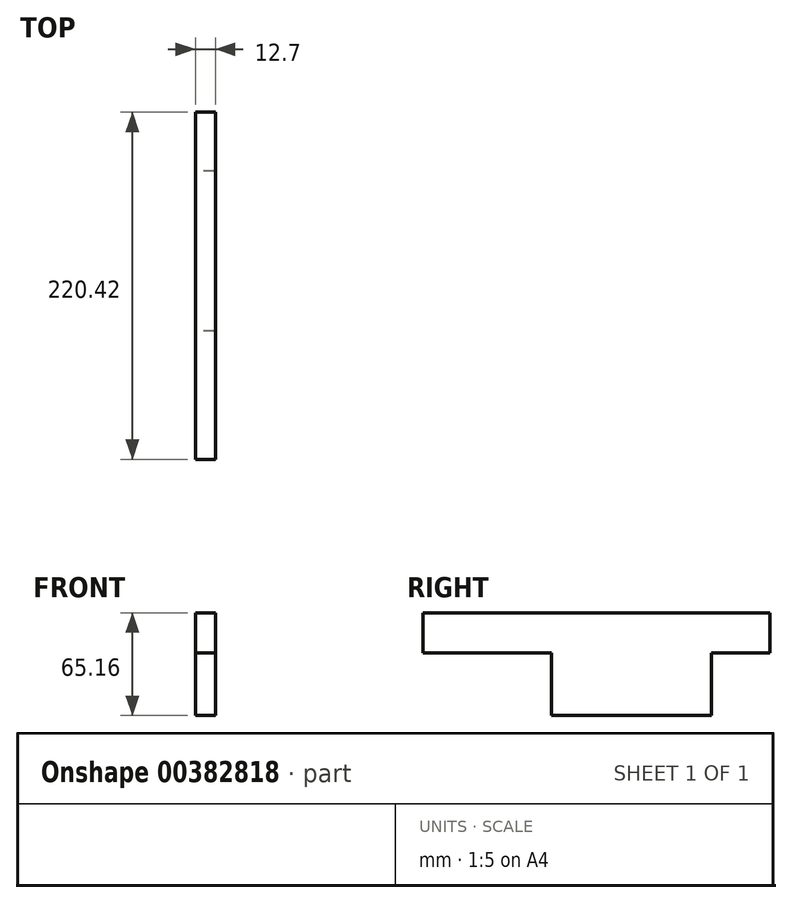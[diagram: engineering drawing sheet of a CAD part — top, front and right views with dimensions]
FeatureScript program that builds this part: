
annotation { "Feature Type Name" : "Feature", "Feature Type Description" : "" }
export const myFeature = defineFeature(function(context is Context, id is Id, definition is map)
    precondition{}
    {
        {
            var Q0;
            Q0=qCreatedBy(makeId("Right.planeOp"),FACE);
            var sketch = newSketch(context, id + "F0", { "sketchPlane" : qUnion([Q0])});
            skLineSegment(sketch, "E0", {"start": v(16.65, 65.16) * mm, "end": v(16.65, 0) * mm});
            skLineSegment(sketch, "E1", {"start": v(16.65, 65.16) * mm, "end": v(118.25, 65.16) * mm});
            skLineSegment(sketch, "E2", {"start": v(118.25, 65.16) * mm, "end": v(118.25, 0) * mm});
            skLineSegment(sketch, "E3", {"start": v(118.25, 0) * mm, "end": v(16.65, 0) * mm});
            skLineSegment(sketch, "E4", {"start": v(16.65, 65.16) * mm, "end": v(-64.92, 65.16) * mm});
            skLineSegment(sketch, "E5", {"start": v(-64.92, 65.16) * mm, "end": v(-64.92, 39.76) * mm});
            skLineSegment(sketch, "E6", {"start": v(-64.92, 39.76) * mm, "end": v(16.65, 39.76) * mm});
            skLineSegment(sketch, "E7", {"start": v(16.65, 39.76) * mm, "end": v(16.65, 65.16) * mm});
            skLineSegment(sketch, "E8", {"start": v(16.65, 39.76) * mm, "end": v(29.35, 39.76) * mm});
            skLineSegment(sketch, "E9", {"start": v(29.35, 39.76) * mm, "end": v(29.35, 20.35) * mm});
            skLineSegment(sketch, "E10", {"start": v(29.35, 20.35) * mm, "end": v(16.65, 20.35) * mm});
            skLineSegment(sketch, "E11", {"start": v(16.65, 20.35) * mm, "end": v(16.65, 39.76) * mm});
            skLineSegment(sketch, "E12", {"start": v(29.35, 39.76) * mm, "end": v(29.35, 52.46) * mm});
            skLineSegment(sketch, "E13", {"start": v(29.35, 52.46) * mm, "end": v(16.65, 52.46) * mm});
            skLineSegment(sketch, "E14", {"start": v(16.65, 39.76) * mm, "end": v(0, 39.76) * mm});
            skLineSegment(sketch, "E15", {"start": v(16.65, 52.46) * mm, "end": v(0, 52.46) * mm});
            skLineSegment(sketch, "E16", {"start": v(0, 52.46) * mm, "end": v(0, 39.76) * mm});
            skLineSegment(sketch, "E17", {"start": v(118.25, 65.16) * mm, "end": v(155.5, 65.16) * mm});
            skLineSegment(sketch, "E18", {"start": v(155.5, 65.16) * mm, "end": v(155.5, 39.76) * mm});
            skLineSegment(sketch, "E19", {"start": v(155.5, 39.76) * mm, "end": v(118.25, 39.76) * mm});
            skLineSegment(sketch, "E20", {"start": v(118.25, 39.76) * mm, "end": v(118.25, 65.16) * mm});
            skLineSegment(sketch, "E21", {"start": v(105.55, 65.16) * mm, "end": v(105.55, 39.76) * mm});
            skLineSegment(sketch, "E22", {"start": v(105.55, 39.76) * mm, "end": v(118.25, 39.76) * mm});
            skLineSegment(sketch, "E23", {"start": v(70.48, 65.16) * mm, "end": v(105.55, 65.16) * mm});
            skLineSegment(sketch, "E24", {"start": v(70.48, 65.16) * mm, "end": v(70.48, 39.14) * mm});
            skLineSegment(sketch, "E25", {"start": v(70.48, 39.14) * mm, "end": v(105.55, 39.76) * mm});
            skLineSegment(sketch, "E26", {"start": v(88.5, 65.16) * mm, "end": v(94.14, 65.16) * mm});
            skSolve(sketch);
        }
        {
            var Q0;
            Q0 = qSketchRegion(id + "F0", true);
            extrude(context, id + "F1", {"entities" : qUnion([Q0]), "depth" : 12.7 * mm});
        }
    });
